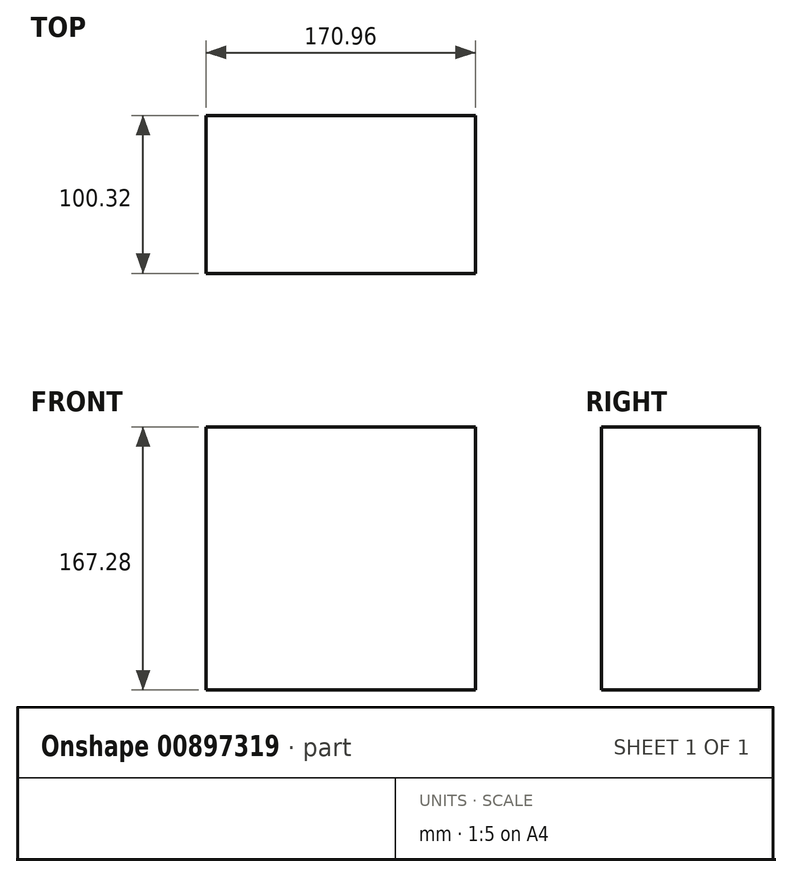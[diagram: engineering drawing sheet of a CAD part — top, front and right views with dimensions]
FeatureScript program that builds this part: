
annotation { "Feature Type Name" : "Feature", "Feature Type Description" : "" }
export const myFeature = defineFeature(function(context is Context, id is Id, definition is map)
    precondition{}
    {
        {
            var Q0;
            Q0=qCreatedBy(makeId("Front.planeOp"),FACE);
            var sketch = newSketch(context, id + "F0", { "sketchPlane" : qUnion([Q0])});
            skLineSegment(sketch, "E0.bottom", {"start": v(-81.76, -73.3) * mm, "end": v(89.2, -73.3) * mm});
            skLineSegment(sketch, "E0.top", {"start": v(-81.76, 93.97) * mm, "end": v(89.2, 93.97) * mm});
            skLineSegment(sketch, "E0.left", {"start": v(-81.76, -73.3) * mm, "end": v(-81.76, 93.97) * mm});
            skLineSegment(sketch, "E0.right", {"start": v(89.2, -73.3) * mm, "end": v(89.2, 93.97) * mm});
            skSolve(sketch);
        }
        {
            var Q0;
            Q0 = qSketchRegion(id + "F0", true);
            var Q1;
            Q1=makeQuery(id+"F0.imprint","IMPRINT",FACE,{"disambiguationData":[TD([[makeQuery(id+"F0.imprint","IMPRINT",EDGE,{"derivedFrom":sQuery(id+"F0.wireOp",EDGE,"E0.bottom")}),1.0]])]});
            extrude(context, id + "F1", {"entities" : qUnion([Q0, Q1]), "depth" : 100.32 * mm, "offsetDistance" : 25.4 * mm});
        }
    });
